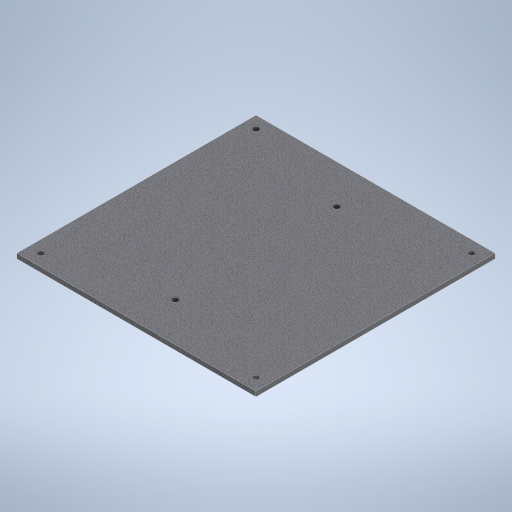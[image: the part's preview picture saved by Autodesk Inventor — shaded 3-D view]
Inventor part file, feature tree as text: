
AUTODESK INVENTOR PART (.ipt)
format: ipt  version: 2023.2 (Build 272271030, 271C)  size: 348,160 bytes
history: native  units: mm
features: sketch x3, hole x2, other x1, extrude x1
ambient origin geometry x8: Origin, YZ Plane, XZ Plane, XY Plane, X Axis, Y Axis, Z Axis, Center Point
bodies: Body1 (feature_tree)
feature tree (7):
  other  "Sólido1"
  extrude  "Extrusão1"  Depth=200.0mm
  hole  "Furo1"  [1 undecoded]
  hole  "Furo2"  [1 undecoded]
  sketch  "Esboço1"  dims[d0=200.0mm d1=200.0mm]
  sketch  "Esboço2"  dims[d2=4.0mm d3=0.0mm d4=10.0mm]
  sketch  "Esboço3"  dims[d5=10.0mm d6=10.0mm d7=10.0mm d8=10.0mm d9=10.0mm d10=10.0mm d11=10.0mm d12=5.0mm d13=6.0mm d14=4.0mm d15=2.0mm d16=90.0deg d17=0.5mm d18=20.594885mm d19=100.0mm d22=0.0mm d27=5.0mm d28=6.0mm d29=4.0mm d30=2.0mm d31=90.0deg d32=0.5mm d33=20.594885mm d34=200.0mm d35=200.0mm d46=200.0mm d47=135.0mm d48=32.5mm]
note: 2 required parameter values undecoded (feature->parameter linkage not recoverable at this tier; creation-order binding heuristic only, values carry confidence <= 0.55)
